# Revit family: Shower-Handshower_Kit-KOHLER-Forte-K-22177_1
name_source: partatom
category: Plumbing Fixtures
units: mm (PartAtom-declared; Revit-internal decimal feet)

## family parameters
Cut with Voids When Loaded = No
Host = Face
OmniClass Number = 23.31.17.00
OmniClass Title = Showers
Part Type = Normal
Room Calculation Point = No
Round Connector Dimension = Use Diameter
Shared = No

## types (5) — shared parameters
ADA Compliant = Yes
Assembly Code = D2010700
CW Connection = No
Cold Water Inlet = Cold Water Inlet
Date Modified = 03/03/2023
Default Elevation = 42"
Drain Included = No
HW Connection = Yes
Height = 31 1/2"
Hot Water Inlet = Hot Water Inlet
Length = 5 5/8"
Manufacturer = Kohler Co.
Master Format 2014 = 22 42 23
Master Format 2014 Name = Residential Showers
Material = Premium Metal Construction
Pressure = 45.00 psi
Product Documentation Link = https://www.us.kohler.com
Product Name = Forte
Product Page URL = http://www.us.kohler.com
Tempered Water Inlet = Tempered Water Inlet
URL = https://www.us.kohler.com
Vent Connection = No
Waste Connection = No
Waste Water Outlet = Waste Water Outlet
Width = 5 7/8"

## per-type parameters (varying)
| type | Description | Finish | Flow Rate | Model | Type | WaterSense Certified |
| 2.5 GPM, BN-Vibrant Brushed Nickel | 2.5 gpm multifunction handshower kit with Katalyst air-induction technology | Kohler-Metal-BN-Vibrant_Brushed_Nickel | 3 GPM | K-22177-BN | 1 | No |
| 2.5 GPM, CP-Polished Chrome | 2.5 gpm multifunction handshower kit with Katalyst air-induction technology | Kohler-Metal-CP-Polished_Chrome | 3 GPM | K-22177-CP | 2 | No |
| 1.75 GPM, BN-Vibrant Brushed Nickel | 1.75 gpm multifunction handshower kit with Katalyst air-induction technology | Kohler-Metal-BN-Vibrant_Brushed_Nickel | 2 GPM | K-22177-G-BN | 3 | Yes |
| 1.75 GPM, CP-Polished Chrome | 1.75 gpm multifunction handshower kit with Katalyst air-induction technology | Kohler-Metal-CP-Polished_Chrome | 2 GPM | K-22177-G-CP | 4 | Yes |
| 1.75 GPM, 0-White | 1.75 gpm multifunction handshower kit with Katalyst air-induction technology | Kohler-Metal-0-White | 2 GPM | K-22177-G-0 | 5 | Yes |

## geometry (parser evidence)
native form markers: Sweep x6
no freeform markers — native parametric forms only
